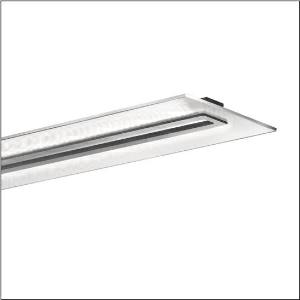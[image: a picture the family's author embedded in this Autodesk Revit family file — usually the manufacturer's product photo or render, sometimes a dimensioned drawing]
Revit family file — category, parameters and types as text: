
# Revit family: vega_r__11_5mn238dle003_bbe2
name_source: partatom
category: Lighting Fixtures
units: mm (PartAtom-declared; Revit-internal decimal feet)

## family parameters
Cut with Voids When Loaded = No
Host = Face
Light Source = No
Part Type = Normal
Room Calculation Point = No
Round Connector Dimension = Use Diameter
Shared = No

## types (1)
- --- (1 x LED 3000K / CRI = 80 (unbekannt), 7300 lm, 3000K)
    Apparent Load = 62 VA
    CIE Flux Codes = 61 86 97 62 100
    Color Rendering = 80
    Color Temperature = 3000K
    Default Elevation = 1800 mm
    Description = Vega® 11, office luminaire, primary light control with prismatic reflector, of PMMA, transparent prismatic structure, CAT 2 (L<= 1500cd/m²), light emission: direct/indirect distribution, primary light characteristic: symmetric, installation type: suspended mounting, surface-mounted, LED, rated luminous flux: 7.300lm, luminous efficacy: 118lm/W, light colour: 830, colour temperature: 3000K, control gear: ECG, with terminal, 3+2-pole, max. 2.5mm², mains connection: 230V, AC, 50Hz, connection cable inclusive, cable length: 1,5m, rated input power: 62W, luminaire housing, rectangular, rounded, of aluminium section, anodised, metallic grey (RAL 9006), length: 1.250mm, width: 350mm, height: 43mm, luminaire housing, lower part, of aluminium section, anodised, metallic grey (RAL 9006), of PC, grey, protection rating (complete): IP20, insulation class (complete): insulation class I (protective earthing), certification: CE, standard: EN 50419, packaging unit: 1 piece
    Height = 40 mm  [stored 0.131234 ft]
    Lamp = 1 x LED 3000K / CRI >= 80 (unbekannt)
    Lamp Light Flux = 7300 lm
    Lamp count = 1
    Length = 1250 mm
    Luminous efficacy = 118 lm/W
    Manufacturer = Siteco
    ModVariant = No
    Model = 5MN238DLE003
    Mounting Place = Ceiling
    Mounting Type = Pendant
    Number of Poles = 1
    OnlyDefault = Yes
    Power Factor = 1
    Product Name = Vega® 11
    Product group = office luminaire | ceiling pendant
    ProductGroupID = 902
    Protection Class = Protection class I
    Protection Degree = IP 20
    RLX_Detail_Level = 1
    RLX_Emergency_Light_Flux = 0 lm
    RLX_Emergency_Type = 0
    RLX_Emergency_Type_DB = No
    RlxData = <blob elided: 62805 chars, md5=b4783c54>
    Socket = socket
    Standby Power = 0 W
    System Light Flux = 7300 lm
    System Power = 62 W
    Type Comments = factory setting: luminous flux: 100 % | dim-lin: 254 | 460 mA
    Type Image = l_1004807.jpg
    URL = http://relux.com
    VarID = @adj_165501
    Voltage = 0 V
    Weight = 0.00 kg
    Width = 350 mm

note: [stored X ft] marks values corroborated as IEEE doubles in the binary element streams (Revit-internal decimal feet)

## geometry (parser evidence)
native form markers: Blend x4, Sweep x9
no freeform markers — native parametric forms only
